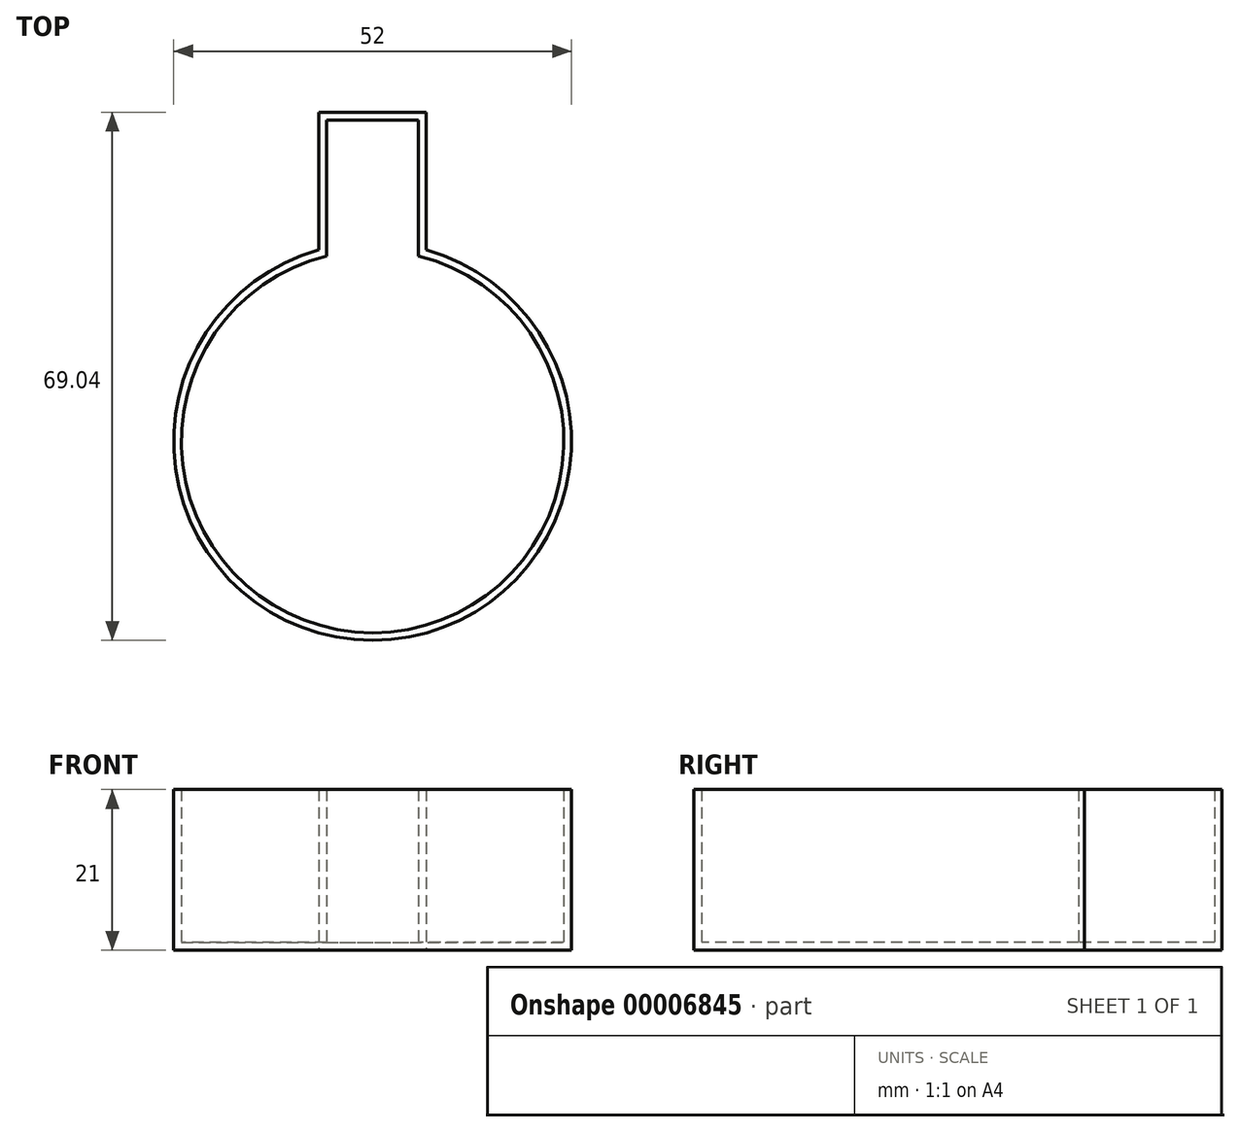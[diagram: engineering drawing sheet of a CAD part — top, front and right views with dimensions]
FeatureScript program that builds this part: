
annotation { "Feature Type Name" : "Feature", "Feature Type Description" : "" }
export const myFeature = defineFeature(function(context is Context, id is Id, definition is map)
    precondition{}
    {
        {
            var Q0;
            Q0=qCreatedBy(makeId("Top.planeOp"),FACE);
            var sketch = newSketch(context, id + "F0", { "sketchPlane" : qUnion([Q0])});
            skArc(sketch, "E0", {"start": v(-7, 25.04) * mm, "mid": v(0, -26) * mm, "end": v(7, 25.04) * mm});
            skLineSegment(sketch, "E1", {"start": v(-7, 43.04) * mm, "end": v(7, 43.04) * mm});
            skPoint(sketch, "E2", {"position": v(0, 43.04) * mm});
            skLineSegment(sketch, "E3", {"start": v(7, 43.04) * mm, "end": v(7, 25.04) * mm});
            skLineSegment(sketch, "E4", {"start": v(-7, 43.04) * mm, "end": v(-7, 25.04) * mm});
            skSolve(sketch);
        }
        {
            var Q0;
            Q0=makeQuery(id+"F0.imprint","IMPRINT",FACE,{"disambiguationData":[TD([[makeQuery(id+"F0.imprint","IMPRINT",EDGE,{"derivedFrom":sQuery(id+"F0.wireOp",EDGE,"E0")}),1.0]])]});
            extrude(context, id + "F1", {"entities" : qUnion([Q0]), "depth" : 1 * mm});
        }
        {
            var Q0;
            Q0=makeQuery(id+"F1.opExtrude","CAP_FACE",FACE,{"disambiguationData":[OSD([sQuery(id+"F0.wireOp",EDGE,"E0"),sQuery(id+"F0.wireOp",EDGE,"E1"),sQuery(id+"F0.wireOp",EDGE,"E3"),sQuery(id+"F0.wireOp",EDGE,"E4")])],"isStart":false});
            var sketch = newSketch(context, id + "F2", { "sketchPlane" : qUnion([Q0])});
            skArc(sketch, "E5.0", {"start": v(-6, 24.27) * mm, "mid": v(0, -25) * mm, "end": v(6, 24.27) * mm});
            skLineSegment(sketch, "E5.1", {"start": v(-6, 42.04) * mm, "end": v(-6, 24.27) * mm});
            skLineSegment(sketch, "E5.2", {"start": v(-6, 42.04) * mm, "end": v(6, 42.04) * mm});
            skLineSegment(sketch, "E5.3", {"start": v(6, 42.04) * mm, "end": v(6, 24.27) * mm});
            skLineSegment(sketch, "E6", {"start": v(0, 0) * mm, "end": v(21.65, -12.5) * mm, "construction": true});
            skLineSegment(sketch, "E7", {"start": v(23, -9.81) * mm, "end": v(17.8, -6.81) * mm});
            skLineSegment(sketch, "E8", {"start": v(17.8, -6.81) * mm, "end": v(14.8, -12) * mm});
            skLineSegment(sketch, "E9", {"start": v(14.8, -12) * mm, "end": v(20, -15) * mm});
            skPoint(sketch, "E10", {"position": v(16.3, -9.4) * mm});
            skLineSegment(sketch, "E11.1.0", {"start": v(-3, 24.82) * mm, "end": v(-3, 18.82) * mm});
            skLineSegment(sketch, "E11.1.1", {"start": v(-3, 18.82) * mm, "end": v(3, 18.82) * mm});
            skLineSegment(sketch, "E11.1.2", {"start": v(3, 18.82) * mm, "end": v(3, 24.82) * mm});
            skLineSegment(sketch, "E11.2.0", {"start": v(-20, -15) * mm, "end": v(-14.8, -12) * mm});
            skLineSegment(sketch, "E11.2.1", {"start": v(-14.8, -12) * mm, "end": v(-17.8, -6.81) * mm});
            skLineSegment(sketch, "E11.2.2", {"start": v(-17.8, -6.81) * mm, "end": v(-23, -9.81) * mm});
            skLineSegment(sketch, "E12", {"start": v(-3, 24.82) * mm, "end": v(3, 24.82) * mm});
            skSolve(sketch);
        }
        {
            var Q0;
            {var subQ1=sQuery(id+"F2.wireOp",EDGE,"E5.1");Q0=makeQuery(id+"F2.imprint","IMPRINT",FACE,{"disambiguationData":[TD([[makeQuery(id+"F2.imprint","IMPRINT",EDGE,{"derivedFrom":subQ1}),-1.0]])]});}
            extrude(context, id + "F3", {"entities" : qUnion([Q0]), "operationType" : NewBodyOperationType.ADD, "depth" : 20 * mm});
        }
    });
